# Revit family: URBANE II 625MM SINGLE TOWEL RAIL
name_source: partatom
category: Specialty Equipment
units: mm (PartAtom-declared; Revit-internal decimal feet)

## family parameters
Cut with Voids When Loaded = No
Host = Face
OmniClass Number = 23.40.20.21.27
OmniClass Title = Towel Bars
Part Type = Normal
Room Calculation Point = No
Round Connector Dimension = Use Radius
Shared = No

## types (5) — shared parameters
Assembly Code = C1030220
Default Elevation = 1000 mm  [stored 3.28084 ft]
Manufacturer = GWA Bathrooms & Kitchens
RailWidth = 600 mm  [stored 1.9685 ft]
URL = https://www.caroma.com.au

## per-type parameters (varying)
| type | Description | Material_Base | Model |
| URBANE II 625MM SINGLE TOWEL RAIL - Chrome | URBANE II 625MM SINGLE TOWEL RAIL - Chrome | GWA_Metal-Chrome | 99625C |
| URBANE II 625MM SINGLE TOWEL RAIL - Matte Black | URBANE II 625MM SINGLE TOWEL RAIL - Matte Black | GWA-Metal-Black | 99625B |
| URBANE II 625MM SINGLE TOWEL RAIL  - Brushed Brass | URBANE II 625MM SINGLE TOWEL RAIL - Brushed Brass | GWA_Metal-Brushed-Brass | 99625BB |
| URBANE II 625MM SINGLE TOWEL RAIL - Gunmetal | URBANE II 625MM SINGLE TOWEL RAIL - Gunmetal | GWA-Metal-Gunmetal Grey | 99625GM |
| URBANE II 625MM SINGLE TOWEL RAIL - Brushed Nickel | URBANE II 625MM SINGLE TOWEL RAIL - Brushed Nickel | GWA_Metal-Brushed-Nickel | 99625BN |

note: [stored X ft] marks values corroborated as IEEE doubles in the binary element streams (Revit-internal decimal feet)

## geometry (parser evidence)
native form markers: Sweep x2
no freeform markers — native parametric forms only
